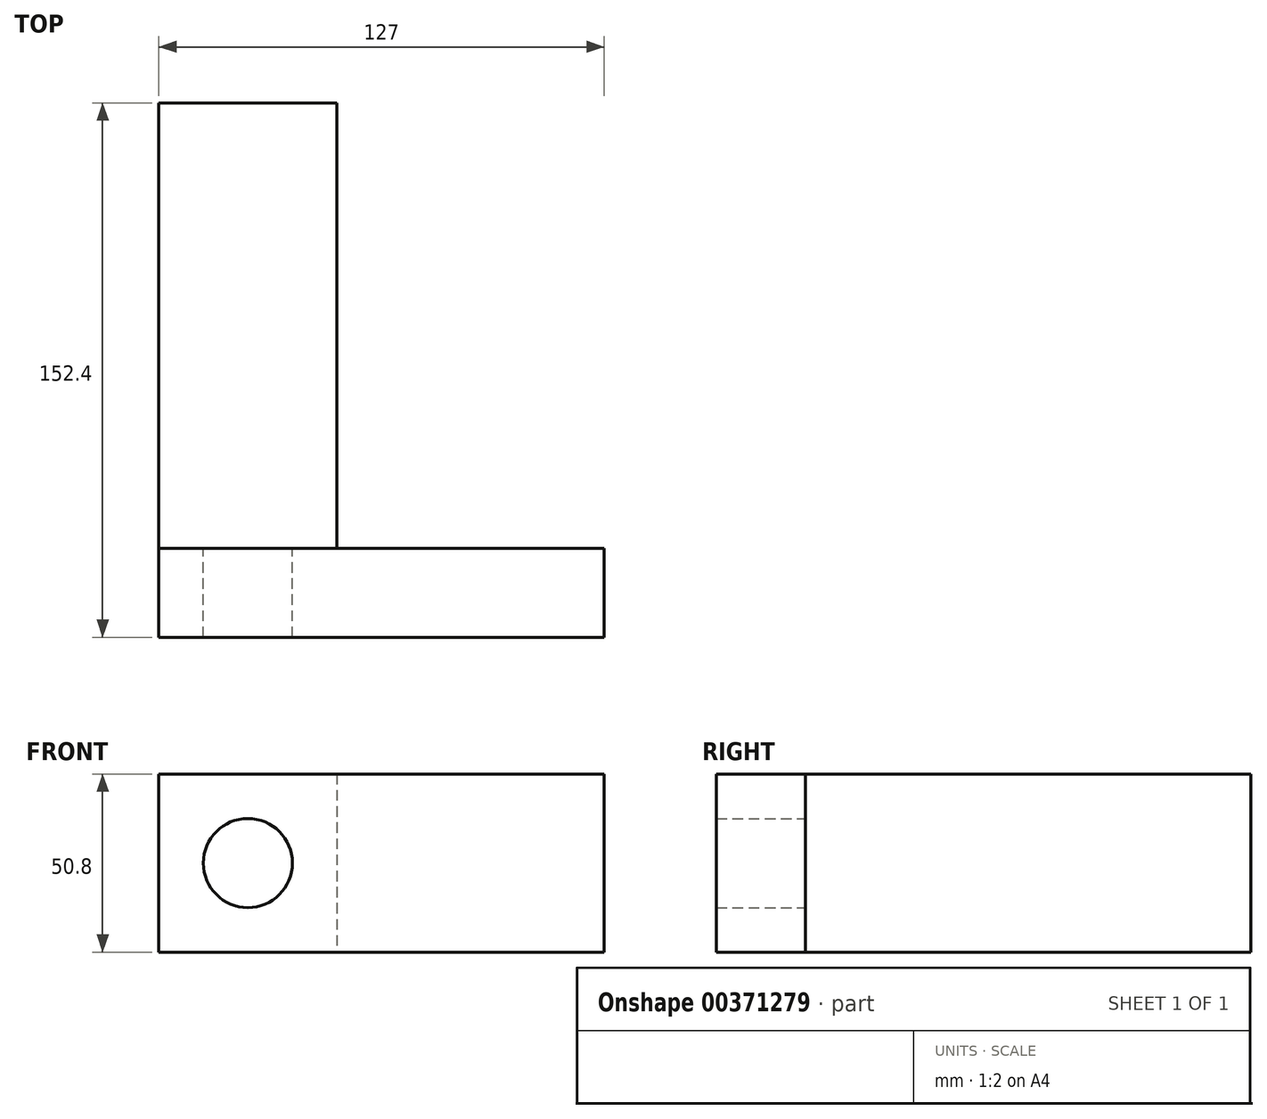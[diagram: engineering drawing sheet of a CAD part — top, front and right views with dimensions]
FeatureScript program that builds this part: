
annotation { "Feature Type Name" : "Feature", "Feature Type Description" : "" }
export const myFeature = defineFeature(function(context is Context, id is Id, definition is map)
    precondition{}
    {
        {
            var Q0;
            Q0=qCreatedBy(makeId("Top.planeOp"),FACE);
            var sketch = newSketch(context, id + "F0", { "sketchPlane" : qUnion([Q0])});
            skLineSegment(sketch, "E0.bottom", {"start": v(-25.4, 63.5) * mm, "end": v(25.4, 63.5) * mm});
            skLineSegment(sketch, "E0.top", {"start": v(-25.4, -63.5) * mm, "end": v(25.4, -63.5) * mm});
            skLineSegment(sketch, "E0.left", {"start": v(-25.4, 63.5) * mm, "end": v(-25.4, -63.5) * mm});
            skLineSegment(sketch, "E0.right", {"start": v(25.4, 63.5) * mm, "end": v(25.4, -63.5) * mm});
            skPoint(sketch, "E1", {"position": v(-25.4, 0) * mm});
            skPoint(sketch, "E2", {"position": v(0, 63.5) * mm});
            skPoint(sketch, "E3", {"position": v(25.4, 0) * mm});
            skPoint(sketch, "E4", {"position": v(0, -63.5) * mm});
            skSolve(sketch);
        }
        {
            var Q0;
            Q0 = qSketchRegion(id + "F0", true);
            extrude(context, id + "F1", {"entities" : qUnion([Q0]), "depth" : 50.8 * mm});
        }
        {
            var Q0;
            Q0=makeQuery(id+"F1.opExtrude","SWEPT_FACE",FACE,{"disambiguationData":[OSD([sQuery(id+"F0.wireOp",EDGE,"E0.top")])]});
            var sketch = newSketch(context, id + "F2", { "sketchPlane" : qUnion([Q0])});
            skPoint(sketch, "E5", {"position": v(0, 25.4) * mm});
            skPoint(sketch, "E5.positionSnap0", {"position": v(-25.4, 25.4) * mm});
            skCircle(sketch, "E6", {"center": v(0, 25.4) * mm, "radius": 12.7 * mm});
            skSolve(sketch);
        }
        {
            var Q0;
            Q0 = qSketchRegion(id + "F2", true);
            extrude(context, id + "F3", {"entities" : qUnion([Q0]), "operationType" : NewBodyOperationType.ADD, "depth" : 25.4 * mm});
        }
        {
            var Q0;
            Q0=makeQuery(id+"F1.opExtrude","SWEPT_FACE",FACE,{"disambiguationData":[OSD([sQuery(id+"F0.wireOp",EDGE,"E0.top")])]});
            var sketch = newSketch(context, id + "F4", { "sketchPlane" : qUnion([Q0])});
            skLineSegment(sketch, "E7.bottom", {"start": v(-25.4, 50.8) * mm, "end": v(101.6, 50.8) * mm});
            skLineSegment(sketch, "E7.top", {"start": v(-25.4, 0) * mm, "end": v(101.6, 0) * mm});
            skLineSegment(sketch, "E7.left", {"start": v(-25.4, 50.8) * mm, "end": v(-25.4, 0) * mm});
            skLineSegment(sketch, "E7.right", {"start": v(101.6, 50.8) * mm, "end": v(101.6, 0) * mm});
            skSolve(sketch);
        }
        {
            var Q0;
            Q0 = qSketchRegion(id + "F4", true);
            extrude(context, id + "F5", {"entities" : qUnion([Q0]), "depth" : 25.4 * mm});
        }
    });
